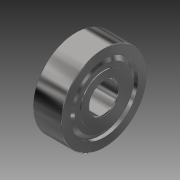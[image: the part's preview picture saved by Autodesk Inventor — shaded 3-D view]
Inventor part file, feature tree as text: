
AUTODESK INVENTOR PART (.ipt)
format: ipt  version: 2018 (Build 220112000, 112)  size: 650,240 bytes
history: native  units: in
note: dims shown in document units (in); Inventor stores cm internally (conversion verified against a paired STEP export)
features: other x11, imported_body x10, extrude x1, fillet x1, sketch x1
ambient origin geometry x8: Origin, YZ Plane, XZ Plane, XY Plane, X Axis, Y Axis, Z Axis, Center Point
bodies: Body1 (feature_tree), Body2 (feature_tree), Body3 (feature_tree), Body4 (feature_tree), Body5 (feature_tree), Body6 (feature_tree), Body7 (feature_tree), Body8 (feature_tree), Body9 (feature_tree), Body10 (feature_tree)
feature tree (24):
  other  "1614ZZ"
  other  "1614ZZ1"
  extrude  "Extrusion1"  Depth=0.01in
  fillet  "Fillet1"  [1 undecoded]
  other  "1614ZZ_1"
  other  "1614ZZ_2"
  other  "1614ZZ_3"
  other  "1614ZZ_4"
  other  "1614ZZ_5"
  other  "1614ZZ_6"
  other  "1614ZZ_7"
  other  "1614ZZ_8"
  other  "1614ZZ_9"
  imported_body  "Base1"
  imported_body  "Base2"
  imported_body  "Base3"
  imported_body  "Base4"
  imported_body  "Base5"
  imported_body  "Base6"
  imported_body  "Base7"
  imported_body  "Base8"
  imported_body  "Base9"
  imported_body  "Base10"
  sketch  "Sketch1"  dims[d0=1.0in d1=0.0in d2=0.01in]
note: 1 required parameter value undecoded (feature->parameter linkage not recoverable at this tier; creation-order binding heuristic only, values carry confidence <= 0.55)
